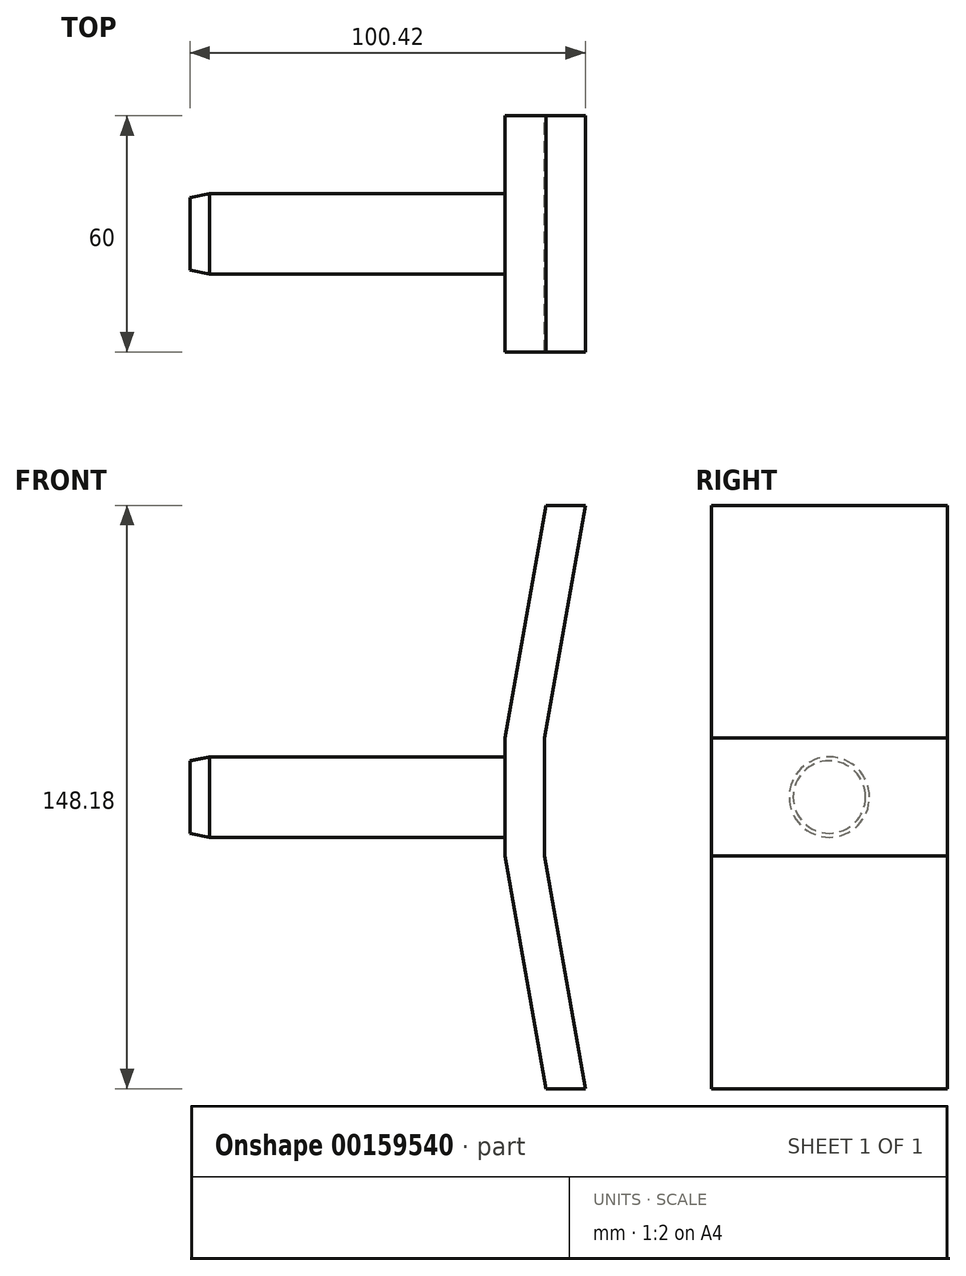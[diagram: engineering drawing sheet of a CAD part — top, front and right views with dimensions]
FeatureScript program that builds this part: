
annotation { "Feature Type Name" : "Feature", "Feature Type Description" : "" }
export const myFeature = defineFeature(function(context is Context, id is Id, definition is map)
    precondition{}
    {
        {
            var Q0;
            Q0=qCreatedBy(makeId("Front.planeOp"),FACE);
            var sketch = newSketch(context, id + "F0", { "sketchPlane" : qUnion([Q0])});
            skLineSegment(sketch, "E0.bottom", {"start": v(-5, 15) * mm, "end": v(5, 15) * mm});
            skLineSegment(sketch, "E0.top", {"start": v(-5, -15) * mm, "end": v(5, -15) * mm});
            skLineSegment(sketch, "E0.left", {"start": v(-5, 15) * mm, "end": v(-5, -15) * mm});
            skLineSegment(sketch, "E0.right", {"start": v(5, 15) * mm, "end": v(5, -15) * mm});
            skPoint(sketch, "E0.middle", {"position": v(0, 0) * mm});
            skLineSegment(sketch, "E1", {"start": v(-5, 15) * mm, "end": v(5.42, 74.09) * mm});
            skLineSegment(sketch, "E2", {"start": v(5.42, 74.09) * mm, "end": v(15.42, 74.09) * mm});
            skLineSegment(sketch, "E3", {"start": v(15.42, 74.09) * mm, "end": v(5, 15) * mm});
            skLineSegment(sketch, "E4", {"start": v(-5, -15) * mm, "end": v(5.42, -74.09) * mm});
            skLineSegment(sketch, "E5", {"start": v(5.42, -74.09) * mm, "end": v(15.42, -74.09) * mm});
            skLineSegment(sketch, "E6", {"start": v(15.42, -74.09) * mm, "end": v(5, -15) * mm});
            skSolve(sketch);
        }
        {
            var Q0;
            Q0 = qSketchRegion(id + "F0", true);
            extrude(context, id + "F1", {"entities" : qUnion([Q0]), "depth" : 60 * mm});
        }
        {
            var Q0;
            Q0=makeQuery(id+"F1.opExtrude","SWEPT_FACE",FACE,{"disambiguationData":[OSD([sQuery(id+"F0.wireOp",EDGE,"E0.left")])]});
            var sketch = newSketch(context, id + "F2", { "sketchPlane" : qUnion([Q0])});
            skCircle(sketch, "E7", {"center": v(30, 0) * mm, "radius": 10.2 * mm});
            skSolve(sketch);
        }
        {
            var Q0;
            {var subQ0=sQuery(id+"F2.wireOp",EDGE,"E7");var subQ1=sQuery(id+"F0.wireOp",EDGE,"E0.left");var subQ2=makeQuery(id+"F2.imprint","INTERSECT",VERTEX,{"derivedFrom":[makeQuery(id+"F1.opExtrude","SWEPT_EDGE",EDGE,{"disambiguationData":[OSD([sQuery(id+"F0.wireOp",EDGE,"E0.bottom"),subQ1,sQuery(id+"F0.wireOp",EDGE,"E1")])]}),subQ0]});Q0=makeQuery(id+"F2.imprint","IMPRINT",FACE,{"disambiguationData":[TD([[makeQuery(id+"F2.imprint","IMPRINT",EDGE,{"disambiguationData":[TD([[subQ2,-1.0]])],"derivedFrom":subQ0}),1.0]])]});}
            extrude(context, id + "F3", {"entities" : qUnion([Q0]), "operationType" : NewBodyOperationType.ADD, "depth" : 80 * mm});
        }
        {
            var Q0;
            Q0=makeQuery(id+"F3.opExtrude","CAP_EDGE",EDGE,{"disambiguationData":[OSD([sQuery(id+"F2.wireOp",EDGE,"E7")])],"isStart":false});
            chamfer(context, id + "F4", {"entities" : qUnion([Q0]), "chamferType" : ChamferType.TWO_OFFSETS, "width1" : 1 * mm, "oppositeDirection" : false, "width2" : 5 * mm, "tangentPropagation" : true});
        }
    });
